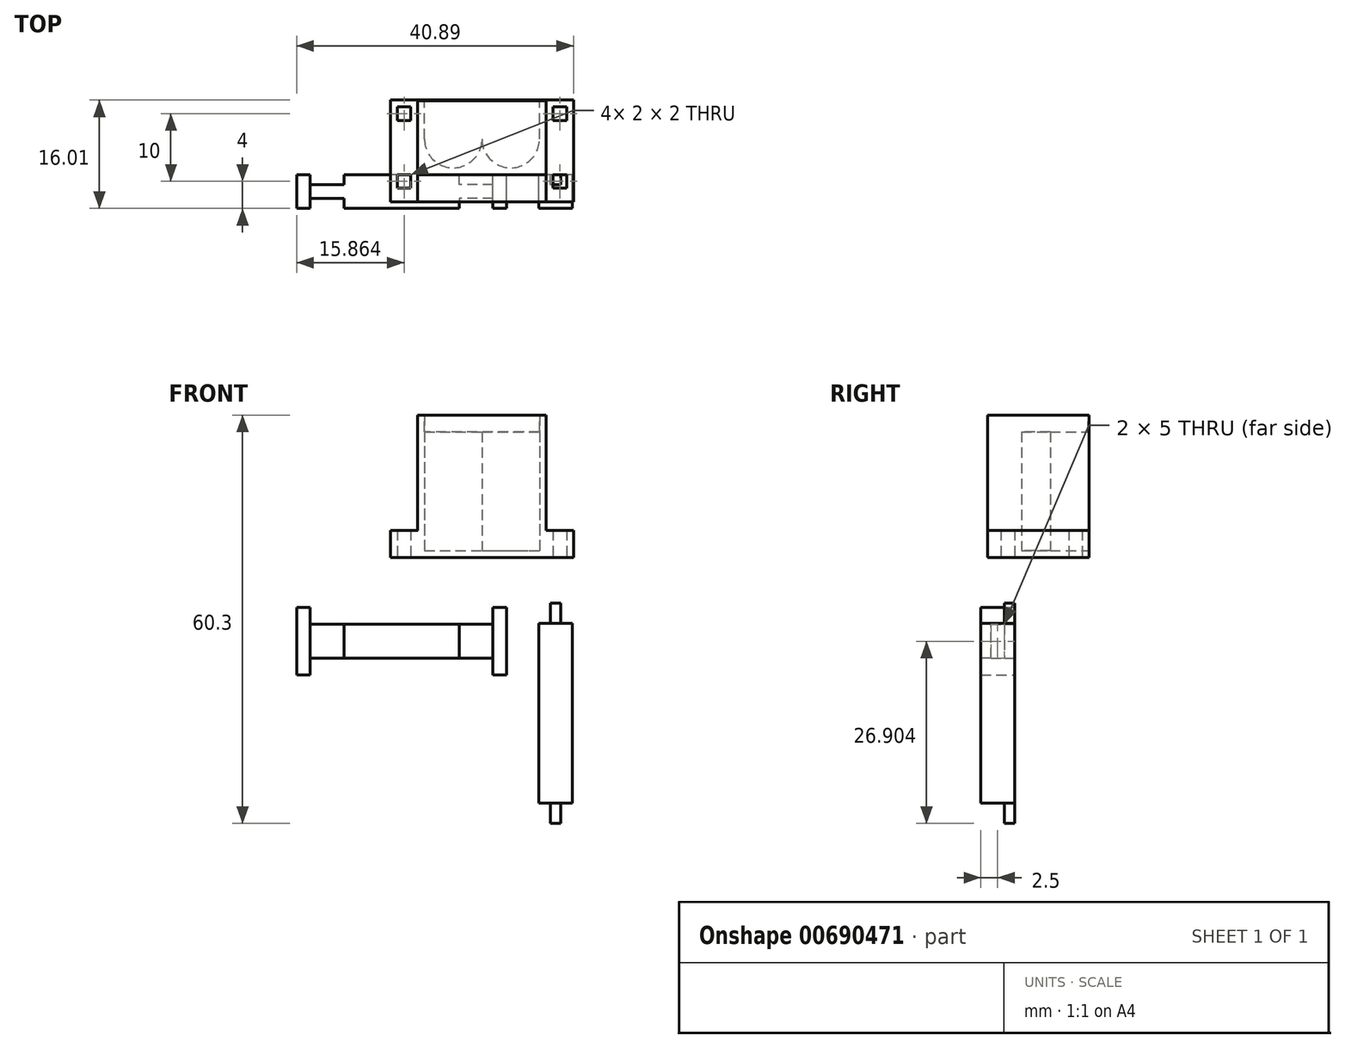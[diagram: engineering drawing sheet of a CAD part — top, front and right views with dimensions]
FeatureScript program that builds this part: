
annotation { "Feature Type Name" : "Feature", "Feature Type Description" : "" }
export const myFeature = defineFeature(function(context is Context, id is Id, definition is map)
    precondition{}
    {
        {
            var Q0;
            Q0=qCreatedBy(makeId("Top.planeOp"),FACE);
            var sketch = newSketch(context, id + "F0", { "sketchPlane" : qUnion([Q0])});
            skCircle(sketch, "E0", {"center": v(-13.07, 5.25) * mm, "radius": 4.25 * mm});
            skCircle(sketch, "E1", {"center": v(-21.57, 5.26) * mm, "radius": 4.25 * mm});
            skLineSegment(sketch, "E2.bottom", {"start": v(-26.82, 11) * mm, "end": v(-7.82, 11) * mm});
            skLineSegment(sketch, "E2.top", {"start": v(-26.82, -4) * mm, "end": v(-7.82, -4) * mm});
            skLineSegment(sketch, "E2.left", {"start": v(-26.82, 11) * mm, "end": v(-26.82, -4) * mm});
            skLineSegment(sketch, "E2.right", {"start": v(-7.82, 11) * mm, "end": v(-7.82, -4) * mm});
            skLineSegment(sketch, "E3.bottom", {"start": v(-25.82, 5.27) * mm, "end": v(-8.82, 5.27) * mm});
            skLineSegment(sketch, "E3.top", {"start": v(-25.82, 11) * mm, "end": v(-8.82, 11) * mm});
            skLineSegment(sketch, "E3.left", {"start": v(-25.82, 5.27) * mm, "end": v(-25.82, 11) * mm});
            skLineSegment(sketch, "E3.right", {"start": v(-8.82, 5.27) * mm, "end": v(-8.82, 11) * mm});
            skSolve(sketch);
        }
        {
            var Q0;
            Q0=makeQuery(id+"F0.imprint","IMPRINT",FACE,{"disambiguationData":[TD([[makeQuery(id+"F0.imprint","IMPRINT",EDGE,{"derivedFrom":sQuery(id+"F0.wireOp",EDGE,"E2.top")}),1.0]])]});
            extrude(context, id + "F1", {"entities" : qUnion([Q0]), "depth" : 20 * mm, "offsetDistance" : 25 * mm});
        }
        {
            var Q0;
            Q0=qCreatedBy(makeId("Front.planeOp"),FACE);
            var sketch = newSketch(context, id + "F2", { "sketchPlane" : qUnion([Q0])});
            skLineSegment(sketch, "E4.bottom", {"start": v(-30.84, 0) * mm, "end": v(-25.84, 0) * mm});
            skLineSegment(sketch, "E4.top", {"start": v(-30.84, -1) * mm, "end": v(-25.84, -1) * mm});
            skLineSegment(sketch, "E4.left", {"start": v(-30.84, 0) * mm, "end": v(-30.84, -1) * mm});
            skLineSegment(sketch, "E4.right", {"start": v(-25.84, 0) * mm, "end": v(-25.84, -1) * mm});
            skLineSegment(sketch, "E5.bottom", {"start": v(-8.81, 0) * mm, "end": v(-3.81, 0) * mm});
            skLineSegment(sketch, "E5.top", {"start": v(-8.81, -1) * mm, "end": v(-3.81, -1) * mm});
            skLineSegment(sketch, "E5.left", {"start": v(-8.81, 0) * mm, "end": v(-8.81, -1) * mm});
            skLineSegment(sketch, "E5.right", {"start": v(-3.81, 0) * mm, "end": v(-3.81, -1) * mm});
            skLineSegment(sketch, "E6.bottom", {"start": v(-25.84, -1) * mm, "end": v(-8.81, -1) * mm});
            skLineSegment(sketch, "E6.top", {"start": v(-25.84, 0) * mm, "end": v(-8.81, 0) * mm});
            skLineSegment(sketch, "E6.left", {"start": v(-25.84, -1) * mm, "end": v(-25.84, 0) * mm});
            skLineSegment(sketch, "E6.right", {"start": v(-8.81, -1) * mm, "end": v(-8.81, 0) * mm});
            skLineSegment(sketch, "E7.bottom", {"start": v(-7.82, 20.01) * mm, "end": v(-26.81, 20.01) * mm});
            skLineSegment(sketch, "E7.top", {"start": v(-7.82, 17.51) * mm, "end": v(-26.81, 17.51) * mm});
            skLineSegment(sketch, "E7.left", {"start": v(-7.82, 20.01) * mm, "end": v(-7.82, 17.51) * mm});
            skLineSegment(sketch, "E7.right", {"start": v(-26.81, 20.01) * mm, "end": v(-26.81, 17.51) * mm});
            skSolve(sketch);
        }
        {
            var Q0;
            Q0 = qSketchRegion(id + "F2", true);
            extrude(context, id + "F3", {"entities" : qUnion([Q0]), "operationType" : NewBodyOperationType.ADD, "oppositeDirection" : true, "depth" : 10.9 * mm, "offsetDistance" : 25 * mm});
        }
        {
            var Q0;
            Q0=makeQuery(id+"F2.imprint","IMPRINT",FACE,{"disambiguationData":[TD([[makeQuery(id+"F2.imprint","IMPRINT",EDGE,{"derivedFrom":sQuery(id+"F2.wireOp",EDGE,"E4.bottom")}),-1.0]])]});
            var Q1;
            Q1=makeQuery(id+"F2.imprint","IMPRINT",FACE,{"disambiguationData":[TD([[makeQuery(id+"F2.imprint","IMPRINT",EDGE,{"derivedFrom":sQuery(id+"F2.wireOp",EDGE,"E5.bottom")}),-1.0]])]});
            var Q2;
            Q2=makeQuery(id+"F2.imprint","IMPRINT",FACE,{"disambiguationData":[TD([[makeQuery(id+"F2.imprint","IMPRINT",EDGE,{"derivedFrom":sQuery(id+"F2.wireOp",EDGE,"E6.bottom")}),1.0]])]});
            extrude(context, id + "F4", {"entities" : qUnion([Q0, Q1, Q2]), "operationType" : NewBodyOperationType.ADD, "oppositeDirection" : true, "depth" : 11 * mm, "offsetDistance" : 25 * mm, "hasSecondDirection" : true, "secondDirectionOppositeDirection" : false, "secondDirectionDepth" : 4 * mm});
        }
        {
            var Q0;
            {var subQ0=sQuery(id+"F2.wireOp",EDGE,"E6.top");var subQ5=sQuery(id+"F2.wireOp",EDGE,"E5.bottom");var subQ9=sQuery(id+"F2.wireOp",EDGE,"E4.bottom");var subQ10=sQuery(id+"F0.wireOp",EDGE,"E2.right");Q0=makeQuery(id+"F4.boolean.opBoolean","SPLIT",FACE,{"disambiguationData":[TD([makeQuery(id+"F1.opExtrude","SWEPT_FACE",FACE,{"disambiguationData":[OSD([subQ10])]})])],"derivedFrom":makeQuery(id+"F4.opExtrude","SWEPT_FACE",FACE,{"disambiguationData":[OSD([subQ9,subQ5,subQ0])]})});}
            var sketch = newSketch(context, id + "F5", { "sketchPlane" : qUnion([Q0])});
            skLineSegment(sketch, "E8.bottom", {"start": v(-3.81, -4) * mm, "end": v(-7.82, -4) * mm});
            skLineSegment(sketch, "E8.top", {"start": v(-3.81, 11) * mm, "end": v(-7.82, 11) * mm});
            skLineSegment(sketch, "E8.left", {"start": v(-3.81, -4) * mm, "end": v(-3.81, 11) * mm});
            skLineSegment(sketch, "E8.right", {"start": v(-7.82, -4) * mm, "end": v(-7.82, 11) * mm});
            skLineSegment(sketch, "E9.bottom", {"start": v(-30.83, 11) * mm, "end": v(-26.8, 11) * mm});
            skLineSegment(sketch, "E9.top", {"start": v(-30.83, -4) * mm, "end": v(-26.8, -4) * mm});
            skLineSegment(sketch, "E9.left", {"start": v(-30.83, 11) * mm, "end": v(-30.83, -4) * mm});
            skLineSegment(sketch, "E9.right", {"start": v(-26.8, 11) * mm, "end": v(-26.8, -4) * mm});
            skSolve(sketch);
        }
        {
            var Q0;
            Q0 = qSketchRegion(id + "F5", true);
            extrude(context, id + "F6", {"entities" : qUnion([Q0]), "operationType" : NewBodyOperationType.ADD, "depth" : 3 * mm, "offsetDistance" : 25 * mm});
        }
        {
            var Q0;
            Q0=makeQuery(id+"F4.opExtrude","SWEPT_FACE",FACE,{"disambiguationData":[OSD([sQuery(id+"F2.wireOp",EDGE,"E4.top"),sQuery(id+"F2.wireOp",EDGE,"E5.top"),sQuery(id+"F2.wireOp",EDGE,"E6.bottom")])]});
            var sketch = newSketch(context, id + "F7", { "sketchPlane" : qUnion([Q0])});
            skLineSegment(sketch, "E10.bottom", {"start": v(-4.81, -10) * mm, "end": v(-6.81, -10) * mm});
            skLineSegment(sketch, "E10.top", {"start": v(-4.81, -8) * mm, "end": v(-6.81, -8) * mm});
            skLineSegment(sketch, "E10.left", {"start": v(-4.81, -10) * mm, "end": v(-4.81, -8) * mm});
            skLineSegment(sketch, "E10.right", {"start": v(-6.81, -10) * mm, "end": v(-6.81, -8) * mm});
            skLineSegment(sketch, "E11.bottom", {"start": v(-4.81, 0) * mm, "end": v(-6.81, 0) * mm});
            skLineSegment(sketch, "E11.top", {"start": v(-4.81, 2) * mm, "end": v(-6.81, 2) * mm});
            skLineSegment(sketch, "E11.left", {"start": v(-4.81, 0) * mm, "end": v(-4.81, 2) * mm});
            skLineSegment(sketch, "E11.right", {"start": v(-6.81, 0) * mm, "end": v(-6.81, 2) * mm});
            skLineSegment(sketch, "E12.bottom", {"start": v(-27.84, 0) * mm, "end": v(-29.84, 0) * mm});
            skLineSegment(sketch, "E12.top", {"start": v(-27.84, 2) * mm, "end": v(-29.84, 2) * mm});
            skLineSegment(sketch, "E12.left", {"start": v(-27.84, 0) * mm, "end": v(-27.84, 2) * mm});
            skLineSegment(sketch, "E12.right", {"start": v(-29.84, 0) * mm, "end": v(-29.84, 2) * mm});
            skLineSegment(sketch, "E13.bottom", {"start": v(-27.84, -10) * mm, "end": v(-29.84, -10) * mm});
            skLineSegment(sketch, "E13.top", {"start": v(-27.84, -8) * mm, "end": v(-29.84, -8) * mm});
            skLineSegment(sketch, "E13.left", {"start": v(-27.84, -10) * mm, "end": v(-27.84, -8) * mm});
            skLineSegment(sketch, "E13.right", {"start": v(-29.84, -10) * mm, "end": v(-29.84, -8) * mm});
            skSolve(sketch);
        }
        {
            var Q0;
            Q0=makeQuery(id+"F7.imprint","IMPRINT",FACE,{"disambiguationData":[TD([[makeQuery(id+"F7.imprint","IMPRINT",EDGE,{"derivedFrom":sQuery(id+"F7.wireOp",EDGE,"E10.bottom")}),-1.0]])]});
            var Q1;
            Q1=makeQuery(id+"F7.imprint","IMPRINT",FACE,{"disambiguationData":[TD([[makeQuery(id+"F7.imprint","IMPRINT",EDGE,{"derivedFrom":sQuery(id+"F7.wireOp",EDGE,"E11.bottom")}),-1.0]])]});
            var Q2;
            Q2=makeQuery(id+"F7.imprint","IMPRINT",FACE,{"disambiguationData":[TD([[makeQuery(id+"F7.imprint","IMPRINT",EDGE,{"derivedFrom":sQuery(id+"F7.wireOp",EDGE,"E12.bottom")}),-1.0]])]});
            var Q3;
            Q3=makeQuery(id+"F7.imprint","IMPRINT",FACE,{"disambiguationData":[TD([[makeQuery(id+"F7.imprint","IMPRINT",EDGE,{"derivedFrom":sQuery(id+"F7.wireOp",EDGE,"E13.bottom")}),-1.0]])]});
            extrude(context, id + "F8", {"entities" : qUnion([Q0, Q1, Q2, Q3]), "operationType" : NewBodyOperationType.REMOVE, "oppositeDirection" : true, "depth" : 5 * mm, "offsetDistance" : 25 * mm});
        }
        {
            var Q0;
            Q0=qCreatedBy(makeId("Front.planeOp"),FACE);
            var sketch = newSketch(context, id + "F9", { "sketchPlane" : qUnion([Q0])});
            skLineSegment(sketch, "E14.bottom", {"start": v(-5.7, -7.73) * mm, "end": v(-7.2, -7.73) * mm});
            skLineSegment(sketch, "E14.top", {"start": v(-5.7, -10.73) * mm, "end": v(-7.2, -10.73) * mm});
            skLineSegment(sketch, "E14.left", {"start": v(-5.7, -7.73) * mm, "end": v(-5.7, -10.73) * mm});
            skLineSegment(sketch, "E14.right", {"start": v(-7.2, -7.73) * mm, "end": v(-7.2, -10.73) * mm});
            skLineSegment(sketch, "E15.bottom", {"start": v(-3.96, -10.73) * mm, "end": v(-8.96, -10.73) * mm});
            skLineSegment(sketch, "E15.top", {"start": v(-3.96, -37.3) * mm, "end": v(-8.96, -37.3) * mm});
            skLineSegment(sketch, "E15.left", {"start": v(-3.96, -10.73) * mm, "end": v(-3.96, -37.3) * mm});
            skLineSegment(sketch, "E15.right", {"start": v(-8.96, -10.73) * mm, "end": v(-8.96, -37.3) * mm});
            skLineSegment(sketch, "E16.bottom", {"start": v(-5.7, -37.3) * mm, "end": v(-7.2, -37.3) * mm});
            skLineSegment(sketch, "E16.top", {"start": v(-5.7, -40.3) * mm, "end": v(-7.2, -40.3) * mm});
            skLineSegment(sketch, "E16.left", {"start": v(-5.7, -37.3) * mm, "end": v(-5.7, -40.3) * mm});
            skLineSegment(sketch, "E16.right", {"start": v(-7.2, -37.3) * mm, "end": v(-7.2, -40.3) * mm});
            skSolve(sketch);
        }
        {
            var Q0;
            Q0 = qSketchRegion(id + "F9", true);
            extrude(context, id + "F10", {"entities" : qUnion([Q0]), "operationType" : NewBodyOperationType.ADD, "depth" : 1.5 * mm, "offsetDistance" : 25 * mm});
        }
        {
            var Q0;
            {var subQ0=sQuery(id+"F9.wireOp",EDGE,"E15.left");Q0=makeQuery(id+"F9.imprint","IMPRINT",FACE,{"disambiguationData":[TD([[makeQuery(id+"F9.imprint","IMPRINT",EDGE,{"derivedFrom":subQ0}),-1.0]])]});}
            extrude(context, id + "F11", {"entities" : qUnion([Q0]), "operationType" : NewBodyOperationType.ADD, "depth" : 5 * mm, "offsetDistance" : 25 * mm});
        }
        {
            var Q0;
            Q0=qCreatedBy(makeId("Front.planeOp"),FACE);
            var sketch = newSketch(context, id + "F12", { "sketchPlane" : qUnion([Q0])});
            skLineSegment(sketch, "E17.bottom", {"start": v(-15.7, -10.89) * mm, "end": v(-42.7, -10.89) * mm});
            skLineSegment(sketch, "E17.top", {"start": v(-15.7, -15.89) * mm, "end": v(-42.7, -15.89) * mm});
            skLineSegment(sketch, "E17.left", {"start": v(-15.7, -10.89) * mm, "end": v(-15.7, -15.89) * mm});
            skLineSegment(sketch, "E17.right", {"start": v(-42.7, -10.89) * mm, "end": v(-42.7, -15.89) * mm});
            skLineSegment(sketch, "E18.bottom", {"start": v(-13.7, -8.39) * mm, "end": v(-15.7, -8.39) * mm});
            skLineSegment(sketch, "E18.top", {"start": v(-13.7, -18.39) * mm, "end": v(-15.7, -18.39) * mm});
            skLineSegment(sketch, "E18.left", {"start": v(-13.7, -8.39) * mm, "end": v(-13.7, -18.39) * mm});
            skLineSegment(sketch, "E18.right", {"start": v(-15.7, -8.39) * mm, "end": v(-15.7, -18.39) * mm});
            skLineSegment(sketch, "E19.bottom", {"start": v(-42.7, -8.39) * mm, "end": v(-44.7, -8.39) * mm});
            skLineSegment(sketch, "E19.top", {"start": v(-42.7, -18.39) * mm, "end": v(-44.7, -18.39) * mm});
            skLineSegment(sketch, "E19.left", {"start": v(-42.7, -8.39) * mm, "end": v(-42.7, -18.39) * mm});
            skLineSegment(sketch, "E19.right", {"start": v(-44.7, -8.39) * mm, "end": v(-44.7, -18.39) * mm});
            skSolve(sketch);
        }
        {
            var Q0;
            {var subQ0=sQuery(id+"F12.wireOp",EDGE,"E17.bottom");Q0=makeQuery(id+"F12.imprint","IMPRINT",FACE,{"disambiguationData":[TD([[makeQuery(id+"F12.imprint","IMPRINT",EDGE,{"derivedFrom":subQ0}),1.0]])]});}
            var Q1;
            {var subQ2=sQuery(id+"F12.wireOp",EDGE,"E18.bottom");Q1=makeQuery(id+"F12.imprint","IMPRINT",FACE,{"disambiguationData":[TD([[makeQuery(id+"F12.imprint","IMPRINT",EDGE,{"derivedFrom":subQ2}),1.0]])]});}
            var Q2;
            {var subQ3=sQuery(id+"F12.wireOp",EDGE,"E19.bottom");Q2=makeQuery(id+"F12.imprint","IMPRINT",FACE,{"disambiguationData":[TD([[makeQuery(id+"F12.imprint","IMPRINT",EDGE,{"derivedFrom":subQ3}),1.0]])]});}
            extrude(context, id + "F13", {"entities" : qUnion([Q0, Q1, Q2]), "depth" : 5 * mm, "offsetDistance" : 25 * mm});
        }
        {
            var Q0;
            Q0=makeQuery(id+"F13.opExtrude","CAP_FACE",FACE,{"disambiguationData":[OSD([sQuery(id+"F12.wireOp",EDGE,"E17.bottom"),sQuery(id+"F12.wireOp",EDGE,"E17.top"),sQuery(id+"F12.wireOp",EDGE,"E18.bottom"),sQuery(id+"F12.wireOp",EDGE,"E18.top"),sQuery(id+"F12.wireOp",EDGE,"E18.left"),sQuery(id+"F12.wireOp",EDGE,"E18.right"),sQuery(id+"F12.wireOp",EDGE,"E19.bottom"),sQuery(id+"F12.wireOp",EDGE,"E19.top"),sQuery(id+"F12.wireOp",EDGE,"E19.left"),sQuery(id+"F12.wireOp",EDGE,"E19.right")])],"isStart":true});
            var sketch = newSketch(context, id + "F14", { "sketchPlane" : qUnion([Q0])});
            skLineSegment(sketch, "E20.bottom", {"start": v(15.7, -10.89) * mm, "end": v(20.7, -10.89) * mm});
            skLineSegment(sketch, "E20.top", {"start": v(15.7, -15.89) * mm, "end": v(20.7, -15.89) * mm});
            skLineSegment(sketch, "E20.left", {"start": v(15.7, -10.89) * mm, "end": v(15.7, -15.89) * mm});
            skLineSegment(sketch, "E20.right", {"start": v(20.7, -10.89) * mm, "end": v(20.7, -15.89) * mm});
            skLineSegment(sketch, "E21.bottom", {"start": v(42.7, -10.89) * mm, "end": v(37.7, -10.89) * mm});
            skLineSegment(sketch, "E21.top", {"start": v(42.7, -15.89) * mm, "end": v(37.7, -15.89) * mm});
            skLineSegment(sketch, "E21.left", {"start": v(42.7, -10.89) * mm, "end": v(42.7, -15.89) * mm});
            skLineSegment(sketch, "E21.right", {"start": v(37.7, -10.89) * mm, "end": v(37.7, -15.89) * mm});
            skSolve(sketch);
        }
        {
            var Q0;
            Q0=makeQuery(id+"F14.imprint","IMPRINT",FACE,{"disambiguationData":[TD([[makeQuery(id+"F14.imprint","IMPRINT",EDGE,{"derivedFrom":sQuery(id+"F14.wireOp",EDGE,"E20.bottom")}),-1.0]])]});
            var Q1;
            Q1=makeQuery(id+"F14.imprint","IMPRINT",FACE,{"disambiguationData":[TD([[makeQuery(id+"F14.imprint","IMPRINT",EDGE,{"derivedFrom":sQuery(id+"F14.wireOp",EDGE,"E21.bottom")}),-1.0]])]});
            extrude(context, id + "F15", {"entities" : qUnion([Q0, Q1]), "operationType" : NewBodyOperationType.REMOVE, "oppositeDirection" : true, "depth" : 1.5 * mm, "offsetDistance" : 25 * mm});
        }
        {
            var Q0;
            Q0=makeQuery(id+"F13.opExtrude","CAP_FACE",FACE,{"disambiguationData":[OSD([sQuery(id+"F12.wireOp",EDGE,"E17.bottom"),sQuery(id+"F12.wireOp",EDGE,"E17.top"),sQuery(id+"F12.wireOp",EDGE,"E18.bottom"),sQuery(id+"F12.wireOp",EDGE,"E18.top"),sQuery(id+"F12.wireOp",EDGE,"E18.left"),sQuery(id+"F12.wireOp",EDGE,"E18.right"),sQuery(id+"F12.wireOp",EDGE,"E19.bottom"),sQuery(id+"F12.wireOp",EDGE,"E19.top"),sQuery(id+"F12.wireOp",EDGE,"E19.left"),sQuery(id+"F12.wireOp",EDGE,"E19.right")])],"isStart":false});
            var sketch = newSketch(context, id + "F16", { "sketchPlane" : qUnion([Q0])});
            skLineSegment(sketch, "E22.bottom", {"start": v(-15.7, -15.89) * mm, "end": v(-20.7, -15.89) * mm});
            skLineSegment(sketch, "E22.top", {"start": v(-15.7, -10.89) * mm, "end": v(-20.7, -10.89) * mm});
            skLineSegment(sketch, "E22.left", {"start": v(-15.7, -15.89) * mm, "end": v(-15.7, -10.89) * mm});
            skLineSegment(sketch, "E22.right", {"start": v(-20.7, -15.89) * mm, "end": v(-20.7, -10.89) * mm});
            skLineSegment(sketch, "E23.bottom", {"start": v(-42.7, -15.89) * mm, "end": v(-37.7, -15.89) * mm});
            skLineSegment(sketch, "E23.top", {"start": v(-42.7, -10.89) * mm, "end": v(-37.7, -10.89) * mm});
            skLineSegment(sketch, "E23.left", {"start": v(-42.7, -15.89) * mm, "end": v(-42.7, -10.89) * mm});
            skLineSegment(sketch, "E23.right", {"start": v(-37.7, -15.89) * mm, "end": v(-37.7, -10.89) * mm});
            skSolve(sketch);
        }
        {
            var Q0;
            Q0=makeQuery(id+"F16.imprint","IMPRINT",FACE,{"disambiguationData":[TD([[makeQuery(id+"F16.imprint","IMPRINT",EDGE,{"derivedFrom":sQuery(id+"F16.wireOp",EDGE,"E22.bottom")}),-1.0]])]});
            var Q1;
            Q1=makeQuery(id+"F16.imprint","IMPRINT",FACE,{"disambiguationData":[TD([[makeQuery(id+"F16.imprint","IMPRINT",EDGE,{"derivedFrom":sQuery(id+"F16.wireOp",EDGE,"E23.bottom")}),-1.0]])]});
            extrude(context, id + "F17", {"entities" : qUnion([Q0, Q1]), "operationType" : NewBodyOperationType.REMOVE, "oppositeDirection" : true, "depth" : 1.5 * mm, "offsetDistance" : 25 * mm});
        }
    });
